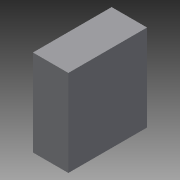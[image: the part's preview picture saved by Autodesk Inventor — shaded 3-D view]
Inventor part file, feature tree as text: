
AUTODESK INVENTOR PART (.ipt)
format: ipt  version: 2014 (Build 180170000, 170)  size: 67,584 bytes
history: native  units: in
note: dims shown in document units (in); Inventor stores cm internally (conversion verified against a paired STEP export)
features: extrude x1, sketch x1
ambient origin geometry x8: Origin, YZ Plane, XZ Plane, XY Plane, X Axis, Y Axis, Z Axis, Center Point
bodies: Solid1 (feature_tree)
feature tree (2):
  extrude  "Extrusion1"  Depth=40.0in
  sketch  "Sketch1"  dims[d0=18.0in d1=40.0in d2=44.0in d3=0.0in]
